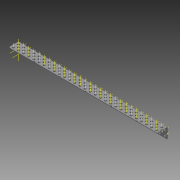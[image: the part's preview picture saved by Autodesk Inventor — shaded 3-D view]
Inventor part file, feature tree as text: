
AUTODESK INVENTOR PART (.ipt)
format: ipt  version: 2015 (Build 190159000, 159)  size: 2,275,328 bytes
history: native  units: in
note: dims shown in document units (in); Inventor stores cm internally (conversion verified against a paired STEP export)
features: other x179, pattern_linear x4, sheet_metal_op x1, extrude x1, imported_body x1, sketch x1
ambient origin geometry x8: Origin, YZ Plane, XZ Plane, XY Plane, X Axis, Y Axis, Z Axis, Center Point
bodies: Body1 (feature_tree)
feature tree (187):
  sheet_metal_op  "Fold1"
  other  "L-Channel"
  extrude  "length cut"  Depth=0.5in
  other  "top out axis"
  other  "top inner axis"
  other  "back out axis"
  other  "back inner axis"
  pattern_linear  "top outer axes"  Count1=2 Spacing1=0.5in
  pattern_linear  "top inner axes"  Spacing1=0.5in  [1 undecoded]
  pattern_linear  "back outer axes"  Count1=2 Spacing1=0.5in
  pattern_linear  "back inner axes"  Spacing1=0.5in  [1 undecoded]
  other  "right plane"
  imported_body  "Base1"
  sketch  "Sketch1"  dims[d1=0.0in d4=0.5in d5=0.7874in d7=0.5in d10=0.5in d13=0.5in d14=0.7874in d16=0.5in d19=0.5in d20=-14.5in d21=0.0in d22=0.0in d23=0.0in d24=0.0in d25=0.0in d26=0.0in]
  other  "Work Point1"
  other  "Work Point2"
  other  "Work Point3"
  other  "Work Point4"
  other  "Work Axis5"
  other  "Work Axis6"
  other  "Work Axis7"
  other  "Work Axis8"
  other  "Work Axis11"
  other  "Work Axis12"
  other  "Work Axis13"
  other  "Work Axis14"
  other  "Work Axis15"
  other  "Work Axis18"
  other  "Work Axis19"
  other  "Work Axis20"
  other  "Work Axis23"
  other  "Work Axis24"
  other  "Work Axis25"
  other  "Work Axis26"
  other  "Work Axis29"
  other  "Work Axis30"
  other  "Work Axis31"
  other  "Work Axis32"
  other  "Work Axis33"
  other  "Work Axis36"
  other  "Work Axis37"
  other  "Work Axis38"
  other  "Work Axis41"
  other  "Work Axis42"
  other  "Work Axis43"
  other  "Work Axis44"
  other  "Work Axis45"
  other  "Work Axis46"
  other  "Work Axis47"
  other  "Work Axis48"
  other  "Work Axis49"
  other  "Work Axis50"
  other  "Work Axis51"
  other  "Work Axis52"
  other  "Work Axis53"
  other  "Work Axis54"
  other  "Work Axis55"
  other  "Work Axis56"
  other  "Work Axis57"
  other  "Work Axis58"
  other  "Work Axis59"
  other  "Work Axis60"
  other  "Work Axis61"
  other  "Work Axis62"
  other  "Work Axis63"
  other  "Work Axis64"
  other  "Work Axis65"
  other  "Work Axis66"
  other  "Work Axis67"
  other  "Work Axis68"
  other  "Work Axis69"
  other  "Work Axis70"
  other  "Work Axis71"
  other  "Work Axis72"
  other  "Work Axis73"
  other  "Work Axis74"
  other  "Work Axis75"
  other  "Work Axis76"
  other  "Work Axis77"
  other  "Work Axis78"
  other  "Work Axis79"
  other  "Work Axis80"
  other  "Work Axis81"
  other  "Work Axis82"
  other  "Work Axis83"
  other  "Work Axis84"
  other  "Work Axis85"
  other  "Work Axis86"
  other  "Work Axis87"
  other  "Work Axis88"
  other  "Work Axis89"
  other  "Work Axis90"
  other  "Work Axis91"
  other  "Work Axis92"
  other  "Work Axis93"
  other  "Work Axis94"
  other  "Work Axis95"
  other  "Work Axis96"
  other  "Work Axis97"
  other  "Work Axis98"
  other  "Work Axis99"
  other  "Work Axis100"
  other  "Work Axis101"
  other  "Work Axis102"
  other  "Work Axis103"
  other  "Work Axis104"
  other  "Work Axis105"
  other  "Work Axis106"
  other  "Work Axis107"
  other  "Work Axis108"
  other  "Work Axis109"
  other  "Work Axis110"
  other  "Work Axis111"
  other  "Work Axis112"
  other  "Work Axis113"
  other  "Work Axis114"
  other  "Work Axis115"
  other  "Work Axis116"
  other  "Work Axis117"
  other  "Work Axis118"
  other  "Work Axis119"
  other  "Work Axis120"
  other  "Work Axis121"
  other  "Work Axis122"
  other  "Work Axis123"
  other  "Work Axis124"
  other  "Work Axis125"
  other  "Work Axis126"
  other  "Work Axis127"
  other  "Work Axis128"
  other  "Work Axis129"
  other  "Work Axis130"
  other  "Work Axis131"
  other  "Work Axis132"
  other  "Work Axis133"
  other  "Work Axis134"
  other  "Work Axis135"
  other  "Work Axis136"
  other  "Work Axis137"
  other  "Work Axis138"
  other  "Work Axis139"
  other  "Work Axis140"
  other  "Work Axis141"
  other  "Work Axis142"
  other  "Work Axis143"
  other  "Work Axis144"
  other  "Work Axis145"
  other  "Work Axis146"
  other  "Work Axis147"
  other  "Work Axis148"
  other  "Work Axis149"
  other  "Work Axis150"
  other  "Work Axis151"
  other  "Work Axis152"
  other  "Work Axis153"
  other  "Work Axis154"
  other  "Work Axis155"
  other  "Work Axis156"
  other  "Work Axis157"
  other  "Work Axis158"
  other  "Work Axis159"
  other  "Work Axis160"
  other  "left plane"
  other  "Work Axis161"
  other  "Work Axis162"
  other  "Work Axis163"
  other  "Work Axis164"
  other  "Work Axis165"
  other  "Work Axis166"
  other  "Work Axis167"
  other  "Work Axis168"
  other  "Work Axis169"
  other  "Work Axis170"
  other  "Work Axis171"
  other  "Work Axis172"
  other  "Work Axis173"
  other  "Work Axis174"
  other  "Work Axis175"
  other  "Work Axis176"
  other  "Work Axis177"
  other  "Work Axis178"
  other  "Work Axis179"
  other  "Work Axis180"
  other  "Work Axis181"
  other  "Work Axis182"
  other  "Work Axis183"
  other  "Work Axis184"
note: 2 required parameter values undecoded (feature->parameter linkage not recoverable at this tier; creation-order binding heuristic only, values carry confidence <= 0.55)
